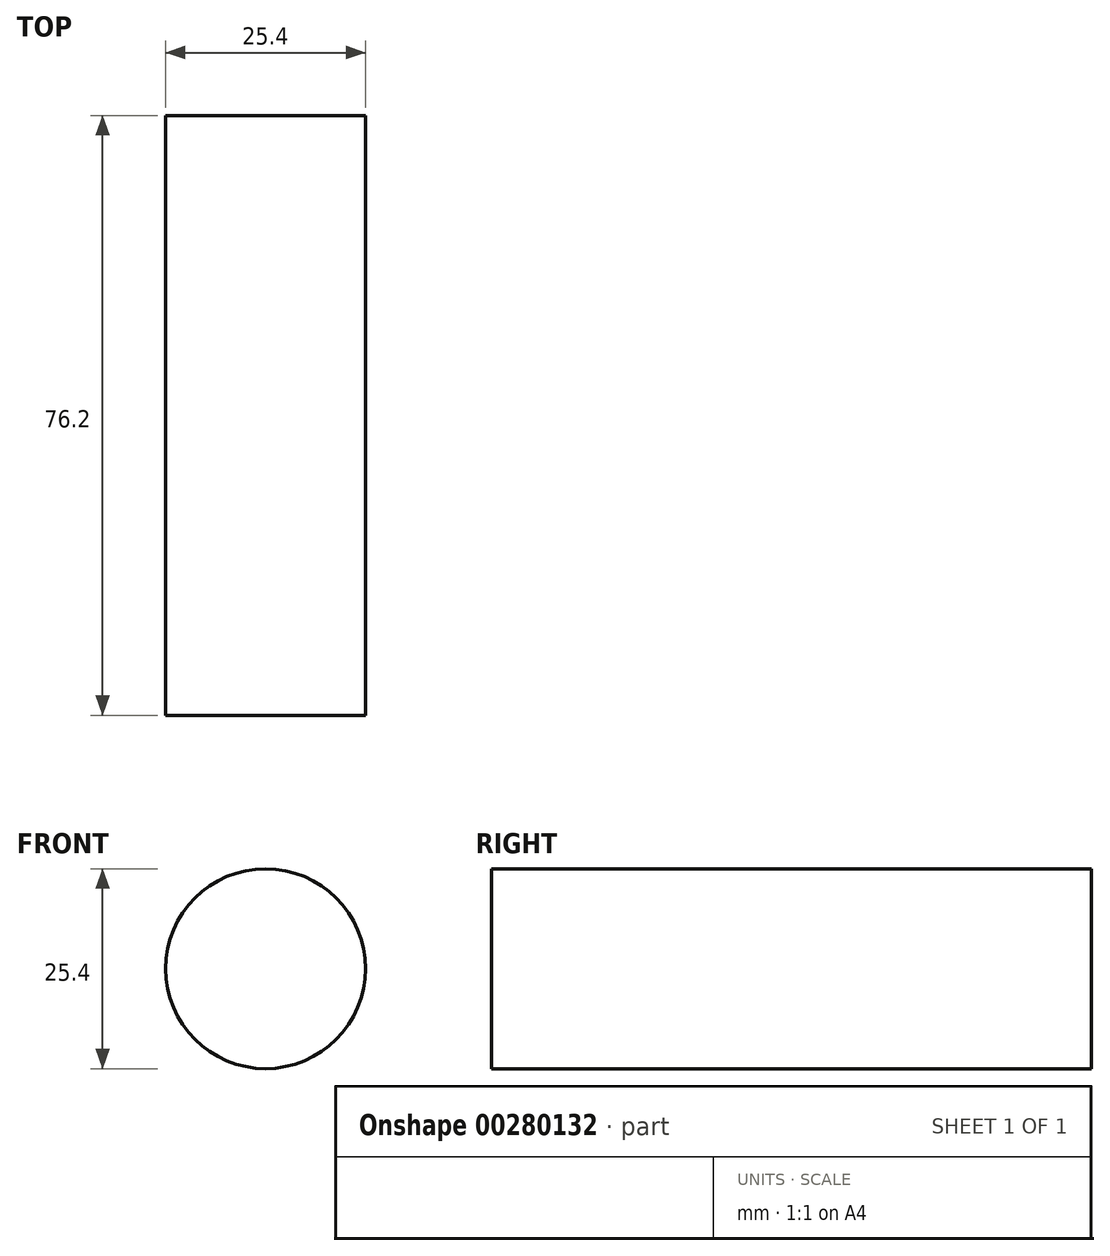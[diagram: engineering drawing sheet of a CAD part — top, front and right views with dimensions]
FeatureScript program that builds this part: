
annotation { "Feature Type Name" : "Feature", "Feature Type Description" : "" }
export const myFeature = defineFeature(function(context is Context, id is Id, definition is map)
    precondition{}
    {
        {
            var Q0;
            Q0=qCreatedBy(makeId("Front.planeOp"),FACE);
            var sketch = newSketch(context, id + "F0", { "sketchPlane" : qUnion([Q0])});
            skCircle(sketch, "E0", {"center": v(-38.2, 34.37) * mm, "radius": 12.7 * mm});
            skSolve(sketch);
        }
        {
            var Q0;
            Q0 = qSketchRegion(id + "F0", true);
            extrude(context, id + "F1", {"entities" : qUnion([Q0]), "depth" : 76.2 * mm});
        }
    });
